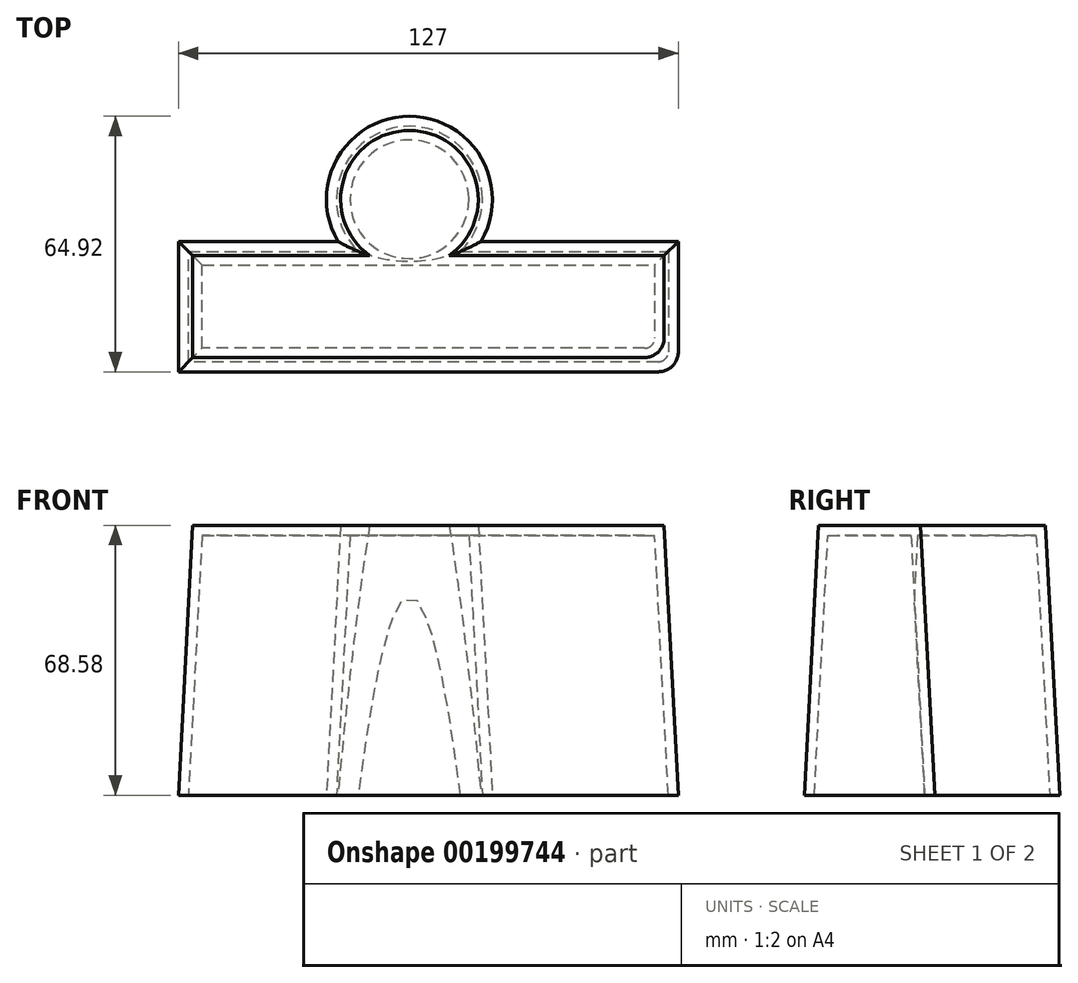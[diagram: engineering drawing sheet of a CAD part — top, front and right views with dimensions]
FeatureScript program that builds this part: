
annotation { "Feature Type Name" : "Feature", "Feature Type Description" : "" }
export const myFeature = defineFeature(function(context is Context, id is Id, definition is map)
    precondition{}
    {
        {
            var Q0;
            Q0=qCreatedBy(makeId("Top.planeOp"),FACE);
            var sketch = newSketch(context, id + "F0", { "sketchPlane" : qUnion([Q0])});
            skLineSegment(sketch, "E0.bottom", {"start": v(0, 0) * mm, "end": v(127, 0) * mm});
            skLineSegment(sketch, "E0.top", {"start": v(0, 33.14) * mm, "end": v(40.53, 33.14) * mm});
            skLineSegment(sketch, "E0.left", {"start": v(0, 0) * mm, "end": v(0, 33.14) * mm});
            skLineSegment(sketch, "E0.right", {"start": v(127, 0) * mm, "end": v(127, 33.14) * mm});
            skArc(sketch, "E1", {"start": v(76.86, 33.14) * mm, "mid": v(58.7, 64.92) * mm, "end": v(40.53, 33.14) * mm});
            skLineSegment(sketch, "E2.trimOffspring", {"start": v(76.86, 33.14) * mm, "end": v(127, 33.14) * mm});
            skSolve(sketch);
        }
        {
            var Q0;
            Q0 = qSketchRegion(id + "F0", true);
            extrude(context, id + "F1", {"entities" : qUnion([Q0]), "depth" : 68.58 * mm, "hasDraft" : true, "draftAngle" : 3 * degree, "draftPullDirection" : true});
        }
        {
            var Q0;
            Q0=makeQuery(id+"F1.opExtrude","SWEPT_EDGE",EDGE,{"disambiguationData":[OSD([sQuery(id+"F0.wireOp",EDGE,"E0.bottom"),sQuery(id+"F0.wireOp",EDGE,"E0.right")])]});
            fillet(context, id + "F2", {"entities" : qUnion([Q0]), "radius" : 5.08 * mm, "tangentPropagation" : true, "allowEdgeOverflow" : false});
        }
        {
            var Q0;
            Q0=makeQuery(id+"F1.opExtrude","CAP_FACE",FACE,{"disambiguationData":[OSD([sQuery(id+"F0.wireOp",EDGE,"E0.bottom"),sQuery(id+"F0.wireOp",EDGE,"E0.top"),sQuery(id+"F0.wireOp",EDGE,"E0.left"),sQuery(id+"F0.wireOp",EDGE,"E0.right")])],"isStart":true});
            shell(context, id + "F3", {"entities" : qUnion([Q0]), "thickness" : 2.54 * mm});
        }
    });
